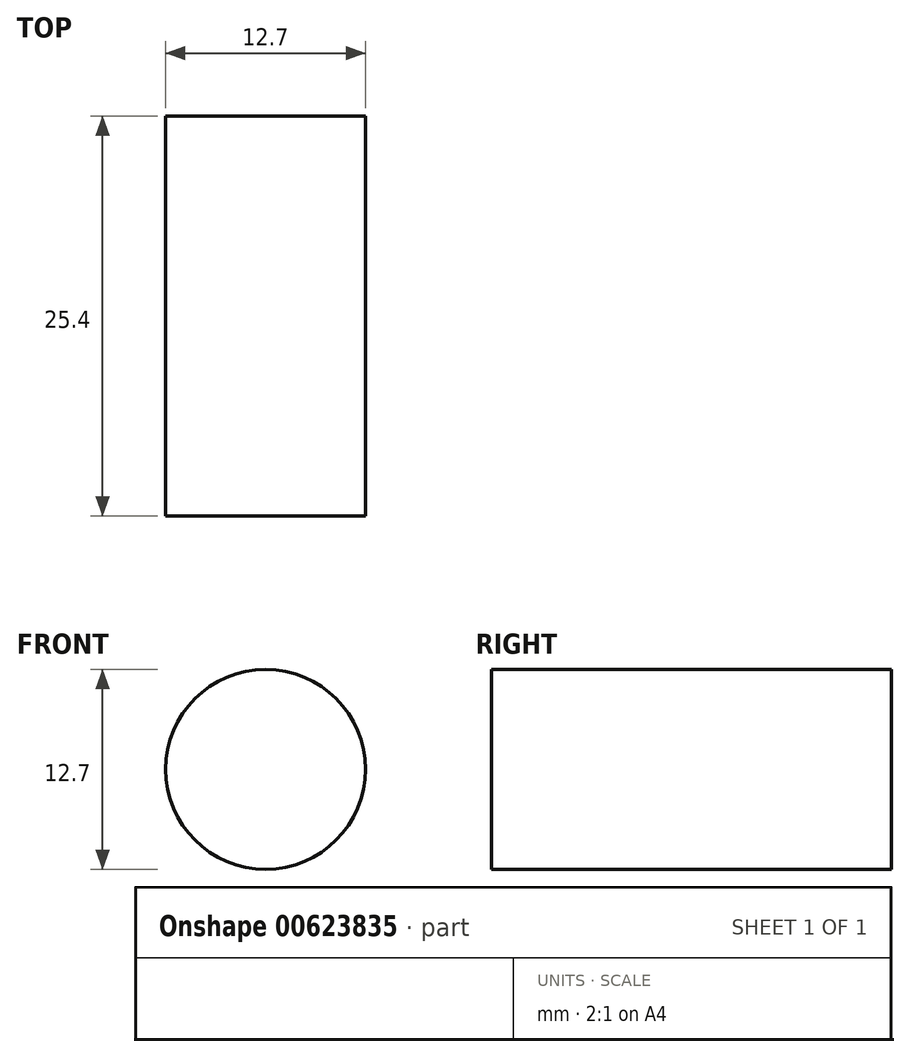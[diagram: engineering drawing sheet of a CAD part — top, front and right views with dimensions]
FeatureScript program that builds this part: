
annotation { "Feature Type Name" : "Feature", "Feature Type Description" : "" }
export const myFeature = defineFeature(function(context is Context, id is Id, definition is map)
    precondition{}
    {
        {
            var Q0;
            Q0=qCreatedBy(makeId("Front.planeOp"),FACE);
            var sketch = newSketch(context, id + "F0", { "sketchPlane" : qUnion([Q0])});
            skCircle(sketch, "E0", {"center": v(-69.17, 37.71) * mm, "radius": 6.35 * mm});
            skSolve(sketch);
        }
        {
            var Q0;
            Q0=makeQuery(id+"F0.imprint","IMPRINT",FACE,{"disambiguationData":[TD([[makeQuery(id+"F0.imprint","IMPRINT",EDGE,{"derivedFrom":sQuery(id+"F0.wireOp",EDGE,"E0")}),1.0]])]});
            extrude(context, id + "F1", {"entities" : qUnion([Q0]), "depth" : 25.4 * mm, "offsetDistance" : 25.4 * mm});
        }
    });
